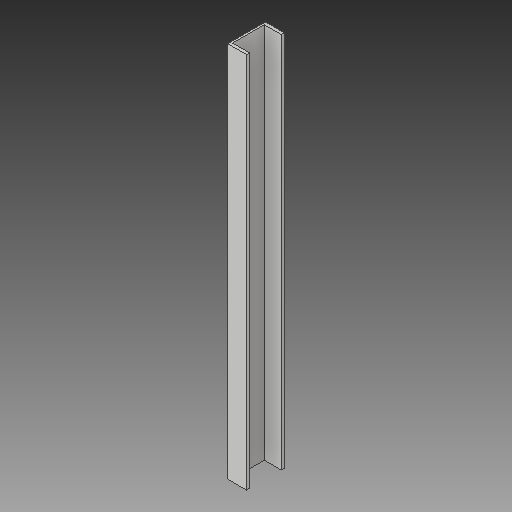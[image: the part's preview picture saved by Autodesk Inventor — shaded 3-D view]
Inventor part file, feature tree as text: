
AUTODESK INVENTOR PART (.ipt)
format: ipt  version: 2019 (Build 230136000, 136)  size: 87,040 bytes
history: native  units: in
note: dims shown in document units (in); Inventor stores cm internally (conversion verified against a paired STEP export)
features: other x3, sketch x1
ambient origin geometry x8: Origin, YZ Plane, XZ Plane, XY Plane, X Axis, Y Axis, Z Axis, Center Point
bodies: Solid1 (feature_tree)
feature tree (4):
  other  "Channel1_MIR.ipt"
  other  "Solid1::Channel1_MIR.ipt"
  other  "TaggingFeature1"
  sketch  "Sketch1"  dims[d0=0.3937in]
